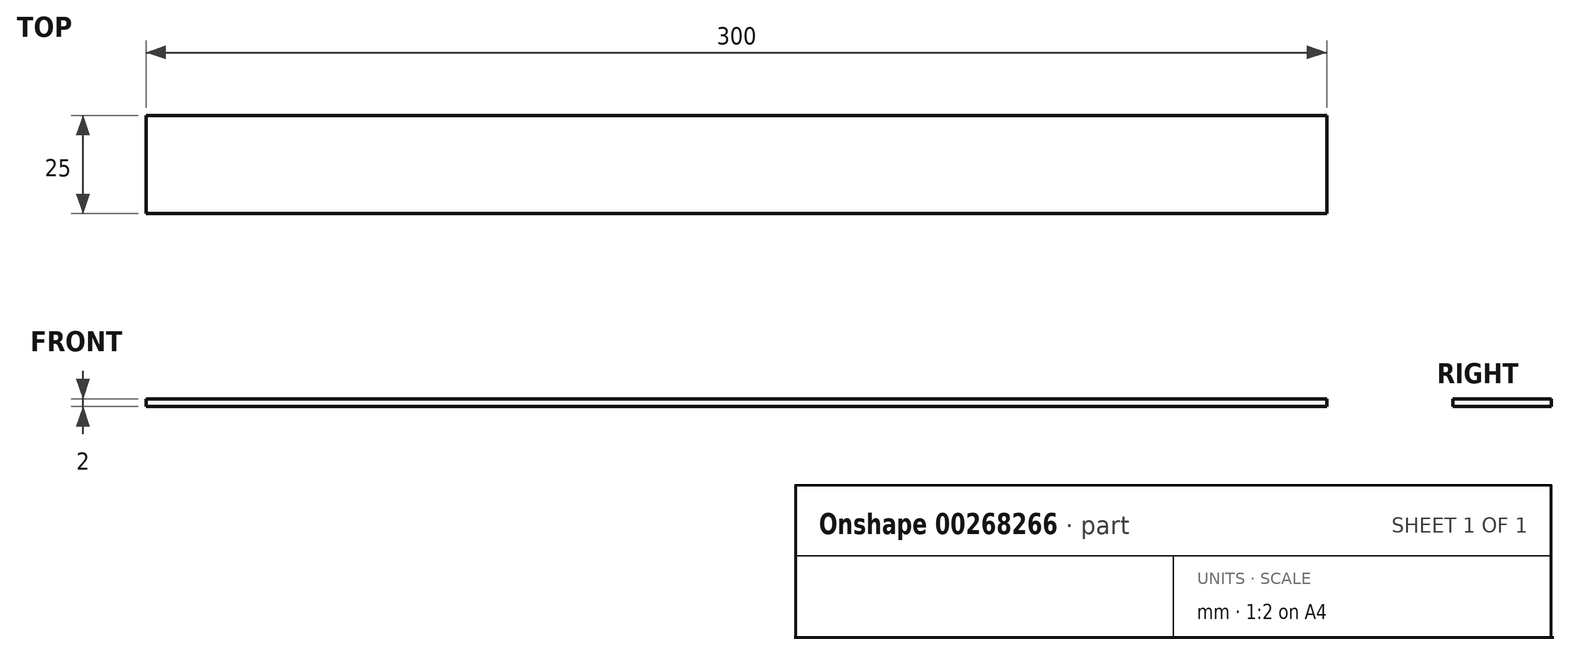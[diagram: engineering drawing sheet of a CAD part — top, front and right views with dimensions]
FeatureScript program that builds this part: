
annotation { "Feature Type Name" : "Feature", "Feature Type Description" : "" }
export const myFeature = defineFeature(function(context is Context, id is Id, definition is map)
    precondition{}
    {
        {
            var Q0;
            Q0=qCreatedBy(makeId("Front.planeOp"),FACE);
            var sketch = newSketch(context, id + "F0", { "sketchPlane" : qUnion([Q0])});
            skLineSegment(sketch, "E0.bottom", {"start": v(0, 0) * mm, "end": v(300, 0) * mm});
            skLineSegment(sketch, "E0.top", {"start": v(0, 2) * mm, "end": v(300, 2) * mm});
            skLineSegment(sketch, "E0.left", {"start": v(0, 0) * mm, "end": v(0, 2) * mm});
            skLineSegment(sketch, "E0.right", {"start": v(300, 0) * mm, "end": v(300, 2) * mm});
            skSolve(sketch);
        }
        {
            var Q0;
            Q0 = qSketchRegion(id + "F0", true);
            extrude(context, id + "F1", {"entities" : qUnion([Q0]), "depth" : 25 * mm, "offsetDistance" : 25 * mm});
        }
    });
